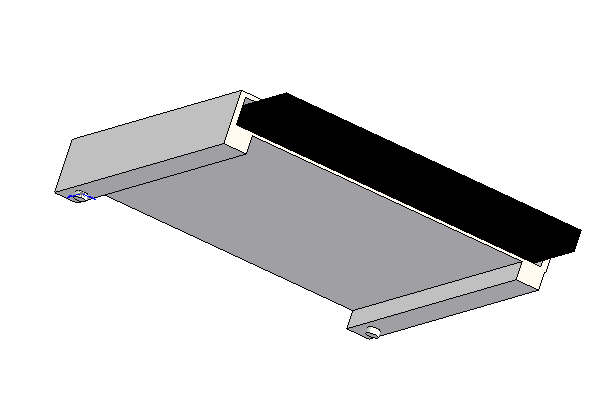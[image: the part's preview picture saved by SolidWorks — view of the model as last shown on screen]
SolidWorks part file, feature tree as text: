
SOLIDWORKS PART (.sldprt)
format: sldprt  version: not decoded by parser v0  size: 124,416 bytes
history: native  units: mm
features: sketch x5, extrude x4, material x1, cut_extrude x1 (+13 scaffold rows collapsed)
feature tree (24):
  scaffold x13  (default folders/planes/origin — collapsed)
  material  "Material <not specified>"
  sketch  "Sketch1"  dims[D1=1.0mm D2=1.0mm D3=26.0mm]
  extrude  "Extrude1"  Depth=0.508mm
  sketch  "Sketch2"  dims[c1.D6=1.0mm c1.D7=1.0mm c1.D1=2.0mm c1.D2=29.1mm c1.D3=1.0mm c1.D4=26.3mm c1.D5=2.0mm c2.D6=26.3mm c2.D7=1.0mm c2.D8=29.1mm]
  extrude  "Extrude2"  Depth=1.5mm
  sketch  "Sketch3"  dims[D1=28.1mm D2=29.1mm]
  extrude  "Extrude3"  Depth=2.9mm
  sketch  "Sketch4"
  cut_extrude  "Cut-Extrude1"  Depth=26.3mm
  sketch  "Sketch5"
  extrude  "Extrude4"  Depth=32.5mm
decode coverage: 8 of 10 modeling features carry decoded parameters
note: suppression state not decoded; provenance and decode notes live in map.json
